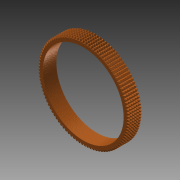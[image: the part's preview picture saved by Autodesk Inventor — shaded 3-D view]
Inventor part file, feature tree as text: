
AUTODESK INVENTOR PART (.ipt)
format: ipt  version: 2014 SP1 (Build 180222100, 222)  size: 4,391,424 bytes
history: native  units: in
note: dims shown in document units (in); Inventor stores cm internally (conversion verified against a paired STEP export)
features: chamfer x2, extrude x1, fillet x1, pattern_circular x1, pattern_linear x1, sketch x1
ambient origin geometry x8: Origin, YZ Plane, XZ Plane, XY Plane, X Axis, Y Axis, Z Axis, Center Point
bodies: Solid1 (feature_tree)
feature tree (7):
  extrude  "Extrusion1"  Depth=0.02in
  chamfer  "Chamfer1"  Distance=0.0247in
  chamfer  "Chamfer2"  Distance=5.8in
  fillet  "Fillet1"  Radius=0.0124in
  pattern_circular  "Circular Pattern1"  [2 undecoded]
  pattern_linear  "Rectangular Pattern1"  Spacing1=0.01in  [1 undecoded]
  sketch  "Sketch1"  dims[d0=5.4in d1=6.09in d2=0.0247in d3=5.8in d4=0.0124in d5=0.06in d6=0.01in d7=0.15in d8=0.0in d9=0.1in d10=0.125in d11=0.1718in d12=0.1in d13=0.125in d14=0.1718in d15=39.3701in d16=360.0deg d18=2.3622in d20=0.15in d21=0.03in d22=0.02in]
note: 3 required parameter values undecoded (feature->parameter linkage not recoverable at this tier; creation-order binding heuristic only, values carry confidence <= 0.55)
